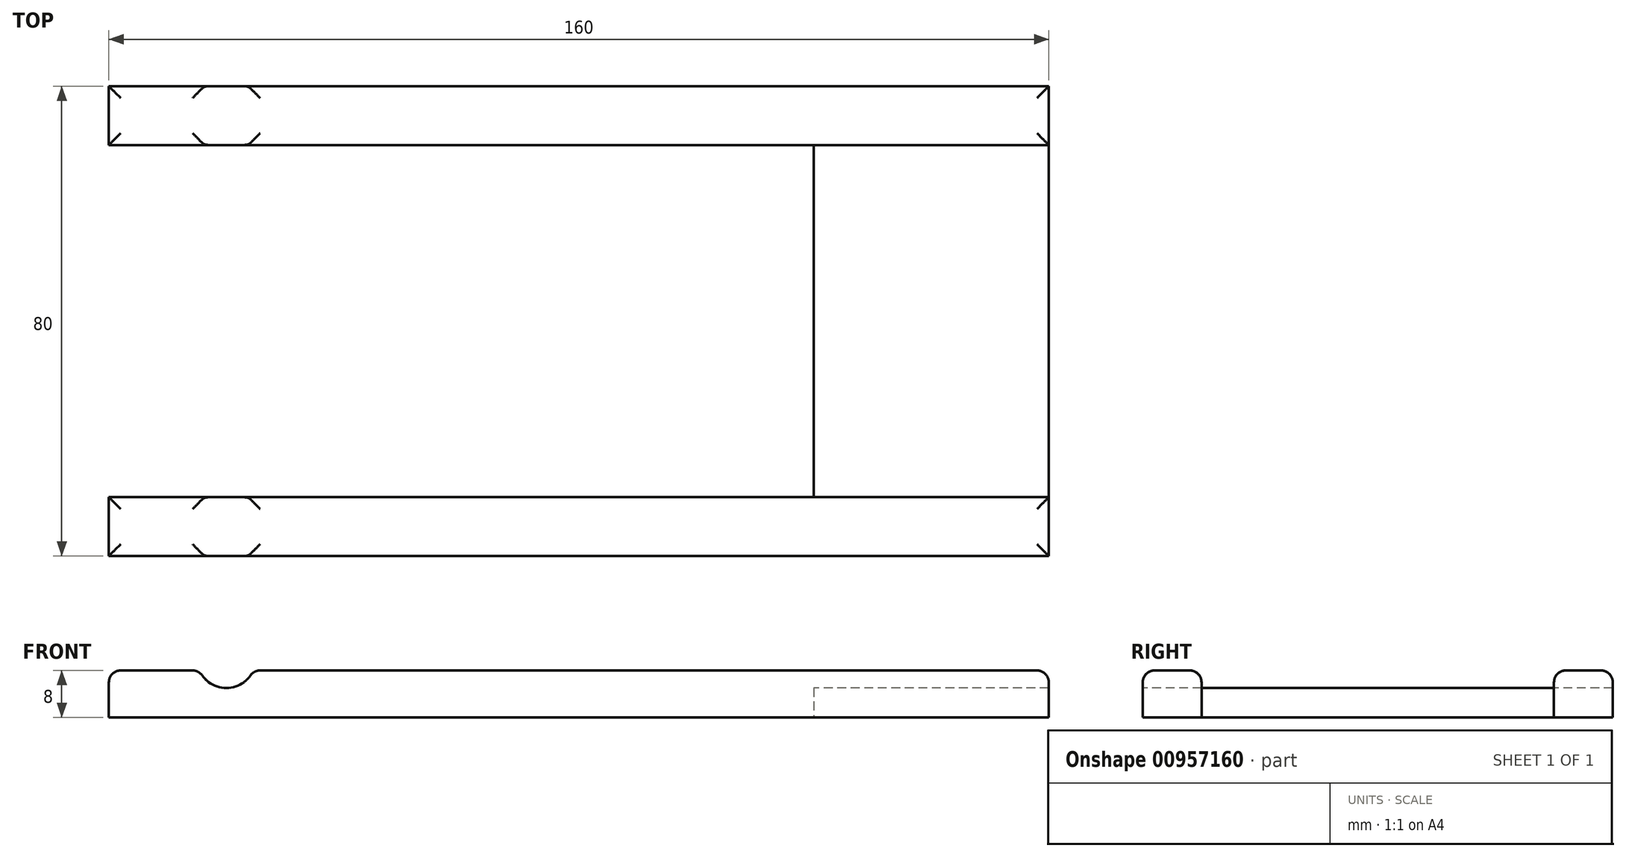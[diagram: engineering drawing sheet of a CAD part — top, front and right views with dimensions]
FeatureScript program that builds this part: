
annotation { "Feature Type Name" : "Feature", "Feature Type Description" : "" }
export const myFeature = defineFeature(function(context is Context, id is Id, definition is map)
    precondition{}
    {
        {
            var Q0;
            Q0=qCreatedBy(makeId("Top.planeOp"),FACE);
            var sketch = newSketch(context, id + "F0", { "sketchPlane" : qUnion([Q0])});
            skLineSegment(sketch, "E0.bottom", {"start": v(0, 0) * mm, "end": v(160, 0) * mm});
            skLineSegment(sketch, "E0.top", {"start": v(0, 10) * mm, "end": v(160, 10) * mm});
            skLineSegment(sketch, "E0.left", {"start": v(0, 0) * mm, "end": v(0, 10) * mm});
            skLineSegment(sketch, "E0.right", {"start": v(160, 0) * mm, "end": v(160, 10) * mm});
            skLineSegment(sketch, "E1.bottom", {"start": v(160, 10) * mm, "end": v(140, 10) * mm});
            skLineSegment(sketch, "E1.top", {"start": v(160, 70) * mm, "end": v(140, 70) * mm});
            skLineSegment(sketch, "E1.left", {"start": v(160, 10) * mm, "end": v(160, 70) * mm});
            skLineSegment(sketch, "E1.right", {"start": v(140, 10) * mm, "end": v(140, 70) * mm});
            skLineSegment(sketch, "E2.bottom", {"start": v(160, 70) * mm, "end": v(0, 70) * mm});
            skLineSegment(sketch, "E2.top", {"start": v(160, 80) * mm, "end": v(0, 80) * mm});
            skLineSegment(sketch, "E2.left", {"start": v(160, 70) * mm, "end": v(160, 80) * mm});
            skLineSegment(sketch, "E2.right", {"start": v(0, 70) * mm, "end": v(0, 80) * mm});
            skSolve(sketch);
        }
        {
            var Q0;
            Q0=makeQuery(id+"F0.imprint","IMPRINT",FACE,{"disambiguationData":[TD([[makeQuery(id+"F0.imprint","IMPRINT",EDGE,{"derivedFrom":sQuery(id+"F0.wireOp",EDGE,"E0.bottom")}),1.0]])]});
            var Q1;
            Q1=makeQuery(id+"F0.imprint","IMPRINT",FACE,{"disambiguationData":[TD([[makeQuery(id+"F0.imprint","IMPRINT",EDGE,{"derivedFrom":sQuery(id+"F0.wireOp",EDGE,"E2.top")}),1.0]])]});
            extrude(context, id + "F1", {"entities" : qUnion([Q0, Q1]), "depth" : 8 * mm, "offsetDistance" : 25 * mm});
        }
        {
            var Q0;
            Q0=qCreatedBy(makeId("Top.planeOp"),FACE);
            var sketch = newSketch(context, id + "F2", { "sketchPlane" : qUnion([Q0])});
            skLineSegment(sketch, "E3", {"start": v(0, 0) * mm, "end": v(160, 0) * mm});
            skLineSegment(sketch, "E4", {"start": v(160, 0) * mm, "end": v(160, 10) * mm});
            skLineSegment(sketch, "E5.bottom", {"start": v(160, 10) * mm, "end": v(120, 10) * mm});
            skLineSegment(sketch, "E5.top", {"start": v(160, 70) * mm, "end": v(120, 70) * mm});
            skLineSegment(sketch, "E5.left", {"start": v(160, 10) * mm, "end": v(160, 70) * mm});
            skLineSegment(sketch, "E5.right", {"start": v(120, 10) * mm, "end": v(120, 70) * mm});
            skSolve(sketch);
        }
        {
            var Q0;
            Q0 = qSketchRegion(id + "F2", true);
            extrude(context, id + "F3", {"entities" : qUnion([Q0]), "depth" : 5 * mm, "offsetDistance" : 25 * mm});
        }
        {
            var Q0;
            Q0=makeQuery(id+"F1.opExtrude","SWEPT_FACE",FACE,{"disambiguationData":[OSD([sQuery(id+"F0.wireOp",EDGE,"E0.bottom")])]});
            var sketch = newSketch(context, id + "F4", { "sketchPlane" : qUnion([Q0])});
            skLineSegment(sketch, "E6", {"start": v(0, 8) * mm, "end": v(20, 8) * mm});
            skLineSegment(sketch, "E7", {"start": v(20, 8) * mm, "end": v(20, 10) * mm});
            skCircle(sketch, "E8", {"center": v(20, 10) * mm, "radius": 5 * mm});
            skSolve(sketch);
        }
        {
            var Q0;
            Q0 = qSketchRegion(id + "F4", true);
            extrude(context, id + "F5", {"entities" : qUnion([Q0]), "operationType" : NewBodyOperationType.REMOVE, "oppositeDirection" : true, "depth" : 500 * mm, "offsetDistance" : 25 * mm});
        }
        {
            var Q0;
            Q0=makeQuery(id+"F1.opExtrude","SWEPT_FACE",FACE,{"disambiguationData":[OSD([sQuery(id+"F0.wireOp",EDGE,"E2.top")])]});
            var sketch = newSketch(context, id + "F6", { "sketchPlane" : qUnion([Q0])});
            skLineSegment(sketch, "E9", {"start": v(0, 8) * mm, "end": v(-20, 8) * mm});
            skLineSegment(sketch, "E10", {"start": v(-20, 8) * mm, "end": v(-20, 10) * mm});
            skCircle(sketch, "E11", {"center": v(-20, 10) * mm, "radius": 5 * mm});
            skSolve(sketch);
        }
        {
            var Q0;
            Q0 = qSketchRegion(id + "F6", true);
            extrude(context, id + "F7", {"entities" : qUnion([Q0]), "operationType" : NewBodyOperationType.REMOVE, "oppositeDirection" : true, "depth" : 25 * mm, "offsetDistance" : 25 * mm});
        }
        {
            var Q0;
            {var subQ0=sQuery(id+"F0.wireOp",EDGE,"E2.bottom");var subQ1=sQuery(id+"F0.wireOp",EDGE,"E2.top");var subQ2=sQuery(id+"F0.wireOp",EDGE,"E2.left");Q0=makeQuery(id+"F7.boolean.opBoolean","SPLIT",FACE,{"disambiguationData":[TD([makeQuery(id+"F1.opExtrude","SWEPT_FACE",FACE,{"disambiguationData":[OSD([subQ2])]})])],"derivedFrom":makeQuery(id+"F1.opExtrude","CAP_FACE",FACE,{"disambiguationData":[OSD([subQ0,subQ1,subQ2,sQuery(id+"F0.wireOp",EDGE,"E2.right")])],"isStart":false})});}
            var Q1;
            {var subQ0=sQuery(id+"F0.wireOp",EDGE,"E2.bottom");var subQ1=sQuery(id+"F0.wireOp",EDGE,"E2.right");var subQ2=sQuery(id+"F0.wireOp",EDGE,"E2.top");Q1=makeQuery(id+"F7.boolean.opBoolean","SPLIT",FACE,{"disambiguationData":[TD([makeQuery(id+"F1.opExtrude","SWEPT_FACE",FACE,{"disambiguationData":[OSD([subQ1])]})])],"derivedFrom":makeQuery(id+"F1.opExtrude","CAP_FACE",FACE,{"disambiguationData":[OSD([subQ0,subQ2,sQuery(id+"F0.wireOp",EDGE,"E2.left"),subQ1])],"isStart":false})});}
            var Q2;
            {var subQ0=sQuery(id+"F0.wireOp",EDGE,"E0.bottom");var subQ1=sQuery(id+"F0.wireOp",EDGE,"E0.right");var subQ2=sQuery(id+"F0.wireOp",EDGE,"E1.bottom");var subQ3=sQuery(id+"F0.wireOp",EDGE,"E0.top");Q2=makeQuery(id+"F5.boolean.opBoolean","SPLIT",FACE,{"disambiguationData":[TD([makeQuery(id+"F1.opExtrude","SWEPT_FACE",FACE,{"disambiguationData":[OSD([subQ1])]})])],"derivedFrom":makeQuery(id+"F1.opExtrude","CAP_FACE",FACE,{"disambiguationData":[OSD([subQ0,subQ3,sQuery(id+"F0.wireOp",EDGE,"E0.left"),subQ1,subQ2])],"isStart":false})});}
            var Q3;
            {var subQ0=sQuery(id+"F0.wireOp",EDGE,"E0.bottom");var subQ1=sQuery(id+"F0.wireOp",EDGE,"E1.bottom");var subQ2=sQuery(id+"F0.wireOp",EDGE,"E0.top");var subQ3=sQuery(id+"F0.wireOp",EDGE,"E0.left");Q3=makeQuery(id+"F5.boolean.opBoolean","SPLIT",FACE,{"disambiguationData":[TD([makeQuery(id+"F1.opExtrude","SWEPT_FACE",FACE,{"disambiguationData":[OSD([subQ3])]})])],"derivedFrom":makeQuery(id+"F1.opExtrude","CAP_FACE",FACE,{"disambiguationData":[OSD([subQ0,subQ2,subQ3,sQuery(id+"F0.wireOp",EDGE,"E0.right"),subQ1])],"isStart":false})});}
            fillet(context, id + "F8", {"entities" : qUnion([Q0, Q1, Q2, Q3]), "radius" : 2 * mm, "tangentPropagation" : true, "allowEdgeOverflow" : false});
        }
    });
